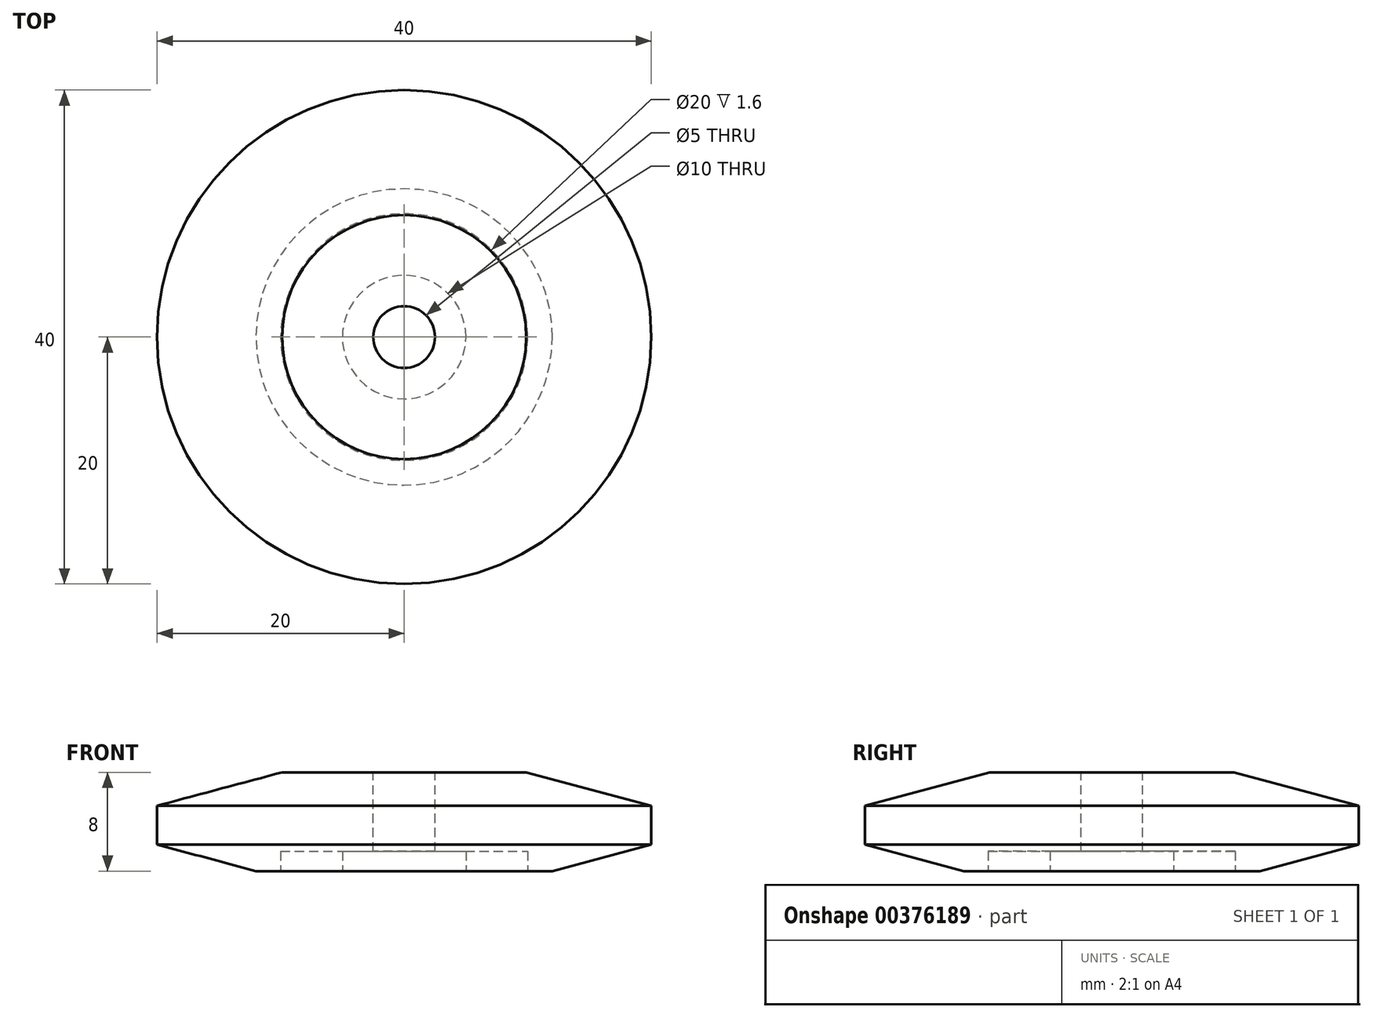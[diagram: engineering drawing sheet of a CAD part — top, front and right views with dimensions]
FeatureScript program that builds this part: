
annotation { "Feature Type Name" : "Feature", "Feature Type Description" : "" }
export const myFeature = defineFeature(function(context is Context, id is Id, definition is map)
    precondition{}
    {
        {
            var Q0;
            Q0=qCreatedBy(makeId("Front.planeOp"),FACE);
            var sketch = newSketch(context, id + "F0", { "sketchPlane" : qUnion([Q0])});
            skLineSegment(sketch, "E0", {"start": v(0, 0) * mm, "end": v(20, 0) * mm});
            skLineSegment(sketch, "E1", {"start": v(20, 0) * mm, "end": v(20, 5.29) * mm});
            skLineSegment(sketch, "E2", {"start": v(0, 0) * mm, "end": v(0, 8) * mm});
            skLineSegment(sketch, "E3", {"start": v(0, 8) * mm, "end": v(9.88, 8) * mm});
            skLineSegment(sketch, "E4", {"start": v(20, 5.29) * mm, "end": v(9.88, 8) * mm});
            skLineSegment(sketch, "E5", {"start": v(9.88, 8) * mm, "end": v(14.52, 8) * mm});
            skLineSegment(sketch, "E6", {"start": v(14.2, 6.84) * mm, "end": v(14.52, 8) * mm});
            skLineSegment(sketch, "E7", {"start": v(0, 0) * mm, "end": v(0, 1.6) * mm});
            skLineSegment(sketch, "E8", {"start": v(10, 1.6) * mm, "end": v(0, 1.6) * mm});
            skLineSegment(sketch, "E9", {"start": v(10, 1.6) * mm, "end": v(10, 0) * mm});
            skLineSegment(sketch, "E10", {"start": v(3, 8) * mm, "end": v(3, 0) * mm, "construction": true});
            skLineSegment(sketch, "E11", {"start": v(12, 0) * mm, "end": v(20, 2.14) * mm});
            skLineSegment(sketch, "E12", {"start": v(5, 1.6) * mm, "end": v(5, 0) * mm});
            skSolve(sketch);
        }
        {
            var Q0;
            {var subQ0=sQuery(id+"F0.wireOp",EDGE,"E9");Q0=makeQuery(id+"F0.imprint","IMPRINT",FACE,{"disambiguationData":[TD([[makeQuery(id+"F0.imprint","IMPRINT",EDGE,{"derivedFrom":subQ0}),-1.0]])]});}
            var Q1;
            Q1=sQuery(id+"F0.wireOp",EDGE,"E7");
            revolve(context, id + "F1", {"entities" : qUnion([Q0]), "axis" : qUnion([Q1]), "revolveType" : RevolveType.FULL});
        }
        {
            var Q0;
            {var subQ9=sQuery(id+"F0.wireOp",EDGE,"E9");Q0=makeQuery(id+"F0.imprint","IMPRINT",FACE,{"disambiguationData":[TD([[makeQuery(id+"F0.imprint","IMPRINT",EDGE,{"derivedFrom":subQ9}),1.0]])]});}
            var Q1;
            {var subQ0=sQuery(id+"F0.wireOp",EDGE,"E7");Q1=makeQuery(id+"F0.imprint","IMPRINT",FACE,{"disambiguationData":[TD([[makeQuery(id+"F0.imprint","IMPRINT",EDGE,{"derivedFrom":subQ0}),-1.0]])]});}
            var Q2;
            Q2=sQuery(id+"F0.wireOp",EDGE,"E2");
            revolve(context, id + "F2", {"entities" : qUnion([Q0, Q1]), "axis" : qUnion([Q2]), "revolveType" : RevolveType.FULL});
        }
        {
            var Q0;
            Q0=makeQuery(id+"F2.opRevolve","SWEPT_FACE",FACE,{"disambiguationData":[OSD([sQuery(id+"F0.wireOp",EDGE,"E3"),sQuery(id+"F0.wireOp",EDGE,"E5")])]});
            var sketch = newSketch(context, id + "F3", { "sketchPlane" : qUnion([Q0])});
            skPoint(sketch, "E13", {"position": v(0, 7) * mm});
            skPoint(sketch, "E14.MirrorP", {"position": v(0, -7) * mm});
            skPoint(sketch, "E15", {"position": v(-9, 0) * mm});
            skPoint(sketch, "E16.MirrorP", {"position": v(9, 0) * mm});
            skPoint(sketch, "E17", {"position": v(0, 0) * mm});
            skSolve(sketch);
        }
        {
            var Q0;
            Q0=sQuery(id+"F3.wireOp",VERTEX,"E17");
            var Q1;
            Q1=makeQuery(id+"F2.opRevolve","SWEPT_BODY",BODY,{"disambiguationData":[OSD([sQuery(id+"F0.wireOp",EDGE,"E0"),sQuery(id+"F0.wireOp",EDGE,"E1"),sQuery(id+"F0.wireOp",EDGE,"E2"),sQuery(id+"F0.wireOp",EDGE,"E3"),sQuery(id+"F0.wireOp",EDGE,"E4"),sQuery(id+"F0.wireOp",EDGE,"E5"),sQuery(id+"F0.wireOp",EDGE,"E6"),sQuery(id+"F0.wireOp",EDGE,"E8"),sQuery(id+"F0.wireOp",EDGE,"E9"),sQuery(id+"F0.wireOp",EDGE,"E11")])]});
            hole(context, id + "F4", {"style" : HoleStyle.SIMPLE, "endStyle" : HoleEndStyle.THROUGH, "standardTappedOrClearance" : lookupTablePath({ "standard" : "ISO", "engagement" : "75%", "pitch" : "1 mm", "size" : "M6", "type" : "Tapped" }), "standardBlindInLast" : lookupTablePath({ "standard" : "ISO", "engagement" : "75%", "pitch" : "1 mm", "size" : "M6", "type" : "Tapped" }), "holeDiameter" : 5 * mm, "showTappedDepth" : true, "isTappedThrough" : true, "tappedDepth" : 35 * mm, "tapClearance" : 3, "startFromSketch" : true, "locations" : qUnion([Q0]), "scope" : qUnion([Q1]), "majorDiameter" : 6 * mm});
        }
    });
